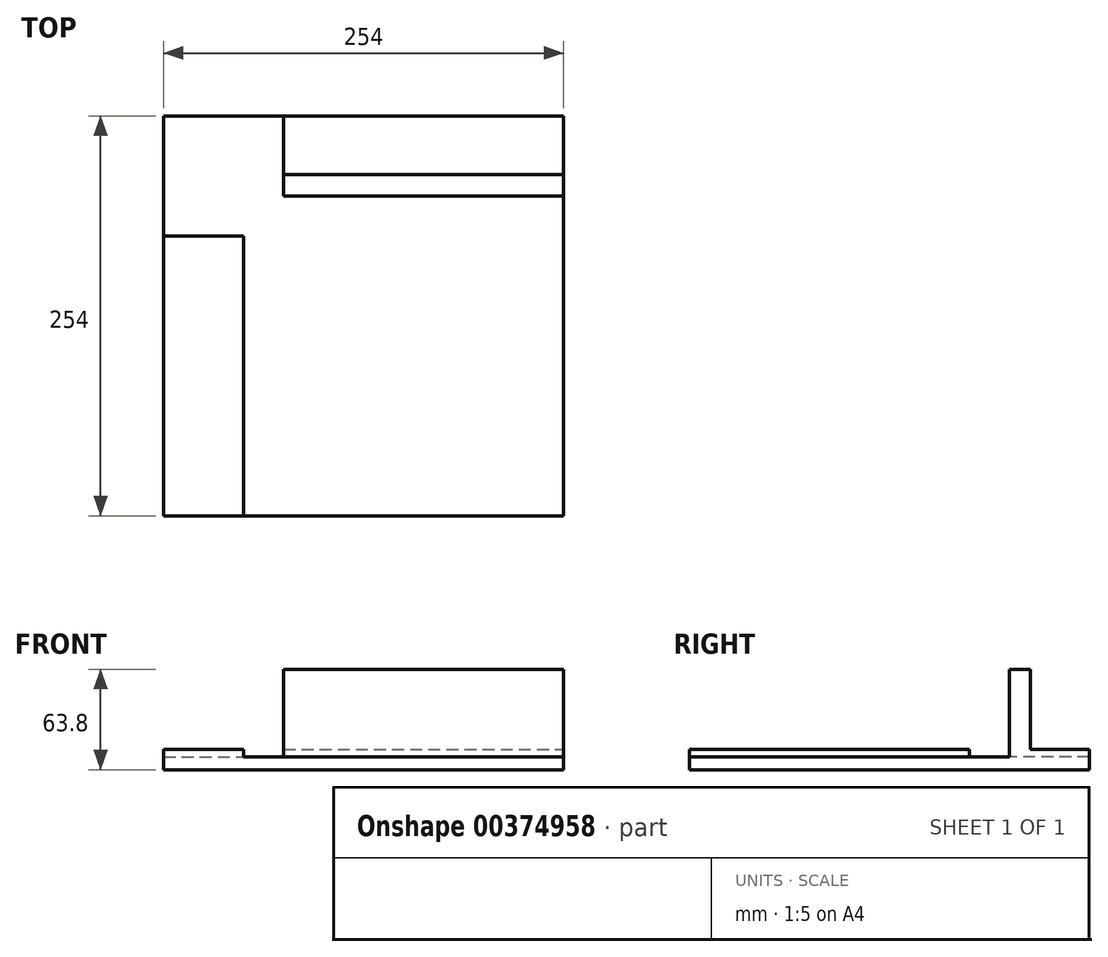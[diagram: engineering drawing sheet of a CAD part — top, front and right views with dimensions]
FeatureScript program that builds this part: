
annotation { "Feature Type Name" : "Feature", "Feature Type Description" : "" }
export const myFeature = defineFeature(function(context is Context, id is Id, definition is map)
    precondition{}
    {
        {
            var Q0;
            Q0=qCreatedBy(makeId("Top.planeOp"),FACE);
            var sketch = newSketch(context, id + "F0", { "sketchPlane" : qUnion([Q0])});
            skLineSegment(sketch, "E0.bottom", {"start": v(-124, 132.62) * mm, "end": v(130, 132.62) * mm});
            skLineSegment(sketch, "E0.top", {"start": v(-124, -121.38) * mm, "end": v(130, -121.38) * mm});
            skLineSegment(sketch, "E0.left", {"start": v(-124, 132.62) * mm, "end": v(-124, -121.38) * mm});
            skLineSegment(sketch, "E0.right", {"start": v(130, 132.62) * mm, "end": v(130, -121.38) * mm});
            skSolve(sketch);
        }
        {
            var Q0;
            Q0 = qSketchRegion(id + "F0", true);
            extrude(context, id + "F1", {"entities" : qUnion([Q0]), "depth" : 8 * mm});
        }
        {
            var Q0;
            Q0=makeQuery(id+"F1.opExtrude","CAP_FACE",FACE,{"disambiguationData":[OSD([sQuery(id+"F0.wireOp",EDGE,"E0.bottom"),sQuery(id+"F0.wireOp",EDGE,"E0.top"),sQuery(id+"F0.wireOp",EDGE,"E0.left"),sQuery(id+"F0.wireOp",EDGE,"E0.right")])],"isStart":false});
            var sketch = newSketch(context, id + "F2", { "sketchPlane" : qUnion([Q0])});
            skLineSegment(sketch, "E1.bottom", {"start": v(-47.8, 132.62) * mm, "end": v(130, 132.62) * mm});
            skLineSegment(sketch, "E1.top", {"start": v(-47.8, 81.82) * mm, "end": v(130, 81.82) * mm});
            skLineSegment(sketch, "E1.left", {"start": v(-47.8, 132.62) * mm, "end": v(-47.8, 81.82) * mm});
            skLineSegment(sketch, "E1.right", {"start": v(130, 132.62) * mm, "end": v(130, 81.82) * mm});
            skSolve(sketch);
        }
        {
            var Q0;
            Q0 = qSketchRegion(id + "F2", true);
            extrude(context, id + "F3", {"entities" : qUnion([Q0]), "operationType" : NewBodyOperationType.ADD, "depth" : 5 * mm});
        }
        {
            var Q0;
            Q0=makeQuery(id+"F1.opExtrude","CAP_FACE",FACE,{"disambiguationData":[OSD([sQuery(id+"F0.wireOp",EDGE,"E0.bottom"),sQuery(id+"F0.wireOp",EDGE,"E0.top"),sQuery(id+"F0.wireOp",EDGE,"E0.left"),sQuery(id+"F0.wireOp",EDGE,"E0.right")])],"isStart":false});
            var sketch = newSketch(context, id + "F4", { "sketchPlane" : qUnion([Q0])});
            skLineSegment(sketch, "E2.bottom", {"start": v(-124, 56.42) * mm, "end": v(-73.2, 56.42) * mm});
            skLineSegment(sketch, "E2.top", {"start": v(-124, -121.38) * mm, "end": v(-73.2, -121.38) * mm});
            skLineSegment(sketch, "E2.left", {"start": v(-124, 56.42) * mm, "end": v(-124, -121.38) * mm});
            skLineSegment(sketch, "E2.right", {"start": v(-73.2, 56.42) * mm, "end": v(-73.2, -121.38) * mm});
            skSolve(sketch);
        }
        {
            var Q0;
            Q0 = qSketchRegion(id + "F4", true);
            extrude(context, id + "F5", {"entities" : qUnion([Q0]), "operationType" : NewBodyOperationType.ADD, "depth" : 5 * mm});
        }
        {
            var Q0;
            Q0=makeQuery(id+"F3.opExtrude","CAP_FACE",FACE,{"disambiguationData":[OSD([sQuery(id+"F2.wireOp",EDGE,"E1.bottom"),sQuery(id+"F2.wireOp",EDGE,"E1.top"),sQuery(id+"F2.wireOp",EDGE,"E1.left"),sQuery(id+"F2.wireOp",EDGE,"E1.right")])],"isStart":false});
            var sketch = newSketch(context, id + "F6", { "sketchPlane" : qUnion([Q0])});
            skLineSegment(sketch, "E3.bottom", {"start": v(-47.8, 95.26) * mm, "end": v(130, 95.26) * mm});
            skLineSegment(sketch, "E3.top", {"start": v(-47.8, 81.82) * mm, "end": v(130, 81.82) * mm});
            skLineSegment(sketch, "E3.left", {"start": v(-47.8, 95.26) * mm, "end": v(-47.8, 81.82) * mm});
            skLineSegment(sketch, "E3.right", {"start": v(130, 95.26) * mm, "end": v(130, 81.82) * mm});
            skSolve(sketch);
        }
        {
            var Q0;
            Q0=makeQuery(id+"F6.imprint","IMPRINT",FACE,{"disambiguationData":[TD([[makeQuery(id+"F6.imprint","IMPRINT",EDGE,{"derivedFrom":sQuery(id+"F6.wireOp",EDGE,"E3.bottom")}),-1.0]])]});
            extrude(context, id + "F7", {"entities" : qUnion([Q0]), "operationType" : NewBodyOperationType.ADD, "depth" : 50.8 * mm});
        }
    });
